# Revit family: Toolflex pidike
name_source: partatom
category: Casework
revit_build: Autodesk Revit 2015 (Build: 20140606_1530(x64)
units: mm (PartAtom-declared; Revit-internal decimal feet)

## types (1)
- 1509
    Depth = 60 mm  [stored 0.19685 ft]
    Height = 16 mm  [stored 0.0524934 ft]
    Keynote = 1509
    Manufacturer = Korpinen
    Model = Toolflex-pidike
    NominalDepth = 0 mm  [stored 0 ft]
    NominalHeight = 0 mm  [stored 0 ft]
    NominalLength = 0 mm  [stored 0 ft]
    URL = http://www.korpinen.com
    Width = 60 mm  [stored 0.19685 ft]
    edge_depth = 1 mm  [stored 0.00328084 ft]
    edge_height = 3 mm  [stored 0.00984252 ft]
    plastic_part = valkoinen muovi
    rubber_part = harmaa kumi
    wall_part_depth = 50 mm  [stored 0.164042 ft]

note: [stored X ft] marks values corroborated as IEEE doubles in the binary element streams (Revit-internal decimal feet)

## geometry (parser evidence)
native form markers: Sweep x2
no freeform markers — native parametric forms only
